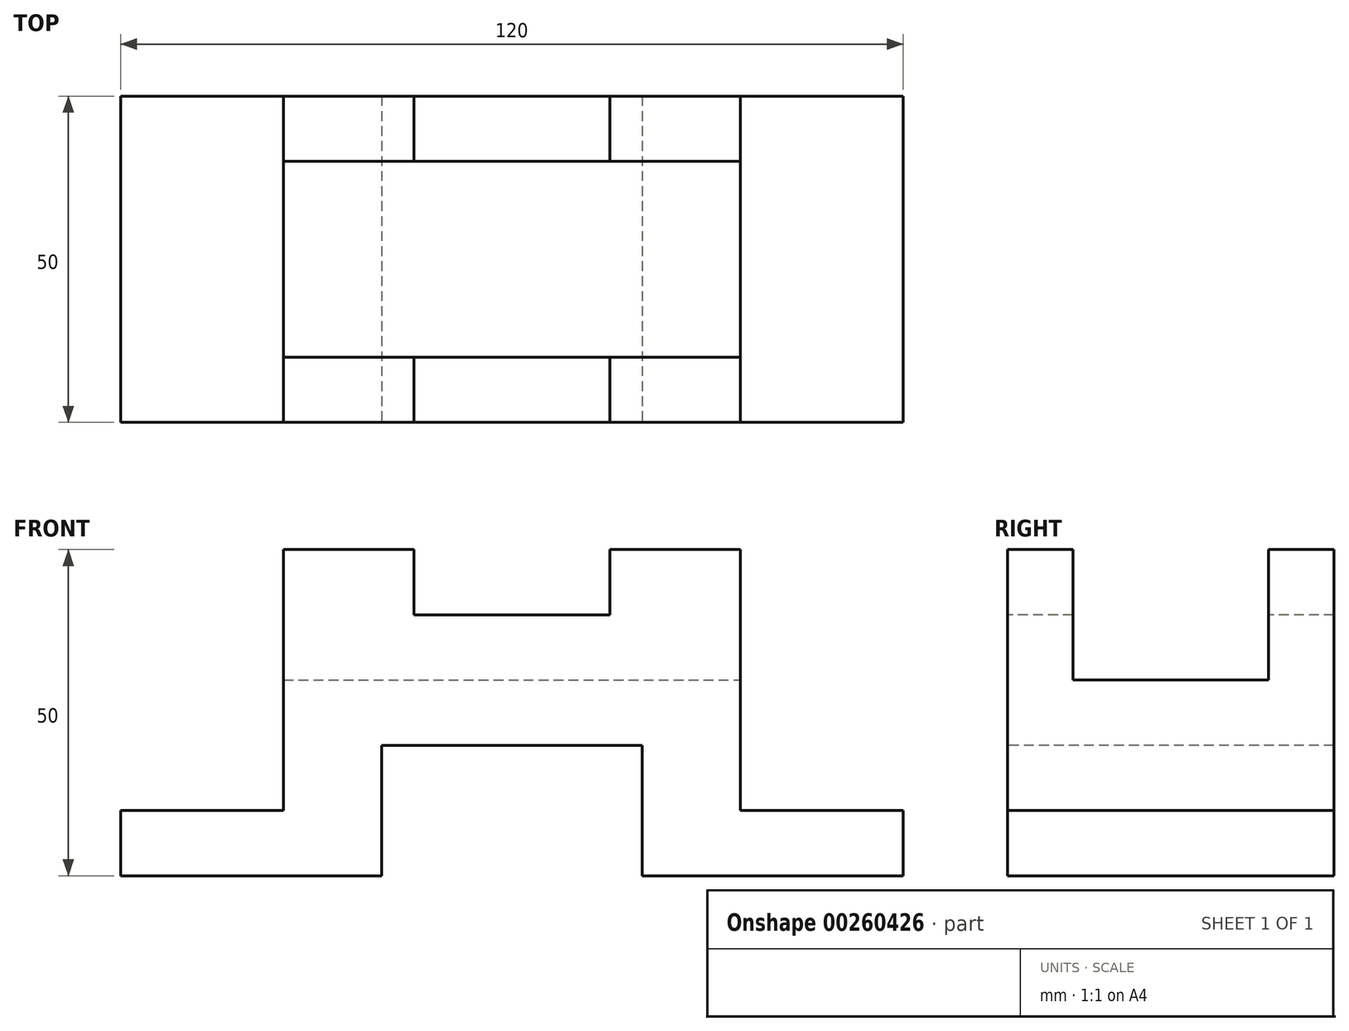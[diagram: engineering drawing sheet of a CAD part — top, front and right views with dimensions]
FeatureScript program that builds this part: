
annotation { "Feature Type Name" : "Feature", "Feature Type Description" : "" }
export const myFeature = defineFeature(function(context is Context, id is Id, definition is map)
    precondition{}
    {
        {
            assignVariable(context, id + "F0", {"name" : "A", "anyValue" : 50});
        }
        {
            var Q0;
            Q0=qCreatedBy(makeId("Front.planeOp"),FACE);
            var sketch = newSketch(context, id + "F1", { "sketchPlane" : qUnion([Q0])});
            skLineSegment(sketch, "E0.bottom", {"start": v(60, 25) * mm, "end": v(-60, 25) * mm});
            skLineSegment(sketch, "E0.top", {"start": v(60, -25) * mm, "end": v(-60, -25) * mm});
            skLineSegment(sketch, "E0.left", {"start": v(60, 25) * mm, "end": v(60, -25) * mm});
            skLineSegment(sketch, "E0.right", {"start": v(-60, 25) * mm, "end": v(-60, -25) * mm});
            skPoint(sketch, "E0.middle", {"position": v(0, 0) * mm});
            skSolve(sketch);
        }
        {
            var Q0;
            Q0=makeQuery(id+"F1.imprint","IMPRINT",FACE,{"disambiguationData":[TD([[makeQuery(id+"F1.imprint","IMPRINT",EDGE,{"derivedFrom":sQuery(id+"F1.wireOp",EDGE,"E0.bottom")}),1.0]])]});
            extrude(context, id + "F2", {"entities" : qUnion([Q0]), "depth" : (getVariable(context, 'A')) * mm});
        }
        {
            var Q0;
            Q0=makeQuery(id+"F2.opExtrude","CAP_FACE",FACE,{"disambiguationData":[OSD([sQuery(id+"F1.wireOp",EDGE,"E0.bottom"),sQuery(id+"F1.wireOp",EDGE,"E0.top"),sQuery(id+"F1.wireOp",EDGE,"E0.left"),sQuery(id+"F1.wireOp",EDGE,"E0.right")])],"isStart":false});
            var sketch = newSketch(context, id + "F3", { "sketchPlane" : qUnion([Q0])});
            skLineSegment(sketch, "E1.bottom", {"start": v(60, 25) * mm, "end": v(35, 25) * mm});
            skLineSegment(sketch, "E1.top", {"start": v(60, -15) * mm, "end": v(35, -15) * mm});
            skLineSegment(sketch, "E1.left", {"start": v(60, 25) * mm, "end": v(60, -15) * mm});
            skLineSegment(sketch, "E1.right", {"start": v(35, 25) * mm, "end": v(35, -15) * mm});
            skLineSegment(sketch, "E2.MirrorCS", {"start": v(-35, 25) * mm, "end": v(-35, -15) * mm});
            skLineSegment(sketch, "E3.MirrorCS", {"start": v(-60, 25) * mm, "end": v(-35, 25) * mm});
            skLineSegment(sketch, "E4.MirrorCS", {"start": v(-60, 25) * mm, "end": v(-60, -15) * mm});
            skLineSegment(sketch, "E5.MirrorCS", {"start": v(-60, -15) * mm, "end": v(-35, -15) * mm});
            skLineSegment(sketch, "E6.bottom", {"start": v(15, 15) * mm, "end": v(-15, 15) * mm});
            skLineSegment(sketch, "E6.left", {"start": v(15, 15) * mm, "end": v(15, 25) * mm});
            skLineSegment(sketch, "E6.right", {"start": v(-15, 15) * mm, "end": v(-15, 25) * mm});
            skPoint(sketch, "E6.middle", {"position": v(0, 25) * mm});
            skLineSegment(sketch, "E7", {"start": v(-15, 25) * mm, "end": v(15, 25) * mm});
            skPoint(sketch, "E8.orphan", {"position": v(-15, 35) * mm});
            skPoint(sketch, "E9.orphan", {"position": v(15, 35) * mm});
            skLineSegment(sketch, "E10.bottom", {"start": v(20, -5) * mm, "end": v(-20, -5) * mm});
            skLineSegment(sketch, "E10.left", {"start": v(20, -5) * mm, "end": v(20, -25) * mm});
            skLineSegment(sketch, "E10.right", {"start": v(-20, -5) * mm, "end": v(-20, -25) * mm});
            skPoint(sketch, "E10.middle", {"position": v(0, -25) * mm});
            skLineSegment(sketch, "E11", {"start": v(-20, -25) * mm, "end": v(20, -25) * mm});
            skPoint(sketch, "E10.top.end.orphan", {"position": v(-20, -45) * mm});
            skPoint(sketch, "E12.orphan", {"position": v(20, -45) * mm});
            skSolve(sketch);
        }
        {
            var Q0;
            Q0=makeQuery(id+"F3.imprint","IMPRINT",FACE,{"disambiguationData":[TD([[makeQuery(id+"F3.imprint","IMPRINT",EDGE,{"derivedFrom":sQuery(id+"F3.wireOp",EDGE,"E2.MirrorCS")}),-1.0]])]});
            var Q1;
            Q1=makeQuery(id+"F3.imprint","IMPRINT",FACE,{"disambiguationData":[TD([[makeQuery(id+"F3.imprint","IMPRINT",EDGE,{"derivedFrom":sQuery(id+"F3.wireOp",EDGE,"E6.bottom")}),-1.0]])]});
            var Q2;
            Q2=makeQuery(id+"F3.imprint","IMPRINT",FACE,{"disambiguationData":[TD([[makeQuery(id+"F3.imprint","IMPRINT",EDGE,{"derivedFrom":sQuery(id+"F3.wireOp",EDGE,"E1.bottom")}),1.0]])]});
            var Q3;
            Q3=makeQuery(id+"F3.imprint","IMPRINT",FACE,{"disambiguationData":[TD([[makeQuery(id+"F3.imprint","IMPRINT",EDGE,{"derivedFrom":sQuery(id+"F3.wireOp",EDGE,"E10.bottom")}),1.0]])]});
            extrude(context, id + "F4", {"entities" : qUnion([Q0, Q1, Q2, Q3]), "operationType" : NewBodyOperationType.REMOVE, "endBound" : BoundingType.UP_TO_NEXT, "oppositeDirection" : true, "depth" : 25 * mm});
        }
        {
            var Q0;
            Q0=makeQuery(id+"F4.boolean.opBoolean","COPY",FACE,{"derivedFrom":makeQuery(id+"F4.opExtrude","SWEPT_FACE",FACE,{"disambiguationData":[OSD([sQuery(id+"F3.wireOp",EDGE,"E1.right")])]})});
            var sketch = newSketch(context, id + "F5", { "sketchPlane" : qUnion([Q0])});
            skLineSegment(sketch, "E13.bottom", {"start": v(-10, 5) * mm, "end": v(-40, 5) * mm});
            skLineSegment(sketch, "E13.left", {"start": v(-10, 5) * mm, "end": v(-10, 25) * mm});
            skLineSegment(sketch, "E13.right", {"start": v(-40, 5) * mm, "end": v(-40, 25) * mm});
            skPoint(sketch, "E13.middle", {"position": v(-25, 25) * mm});
            skLineSegment(sketch, "E14", {"start": v(-40, 25) * mm, "end": v(-10, 25) * mm});
            skPoint(sketch, "E15.orphan", {"position": v(-40, 45) * mm});
            skPoint(sketch, "E16.orphan", {"position": v(-10, 45) * mm});
            skSolve(sketch);
        }
        {
            var Q0;
            Q0=makeQuery(id+"F5.imprint","IMPRINT",FACE,{"disambiguationData":[TD([[makeQuery(id+"F5.imprint","IMPRINT",EDGE,{"derivedFrom":sQuery(id+"F5.wireOp",EDGE,"E13.bottom")}),-1.0]])]});
            extrude(context, id + "F6", {"entities" : qUnion([Q0]), "operationType" : NewBodyOperationType.REMOVE, "endBound" : BoundingType.THROUGH_ALL, "oppositeDirection" : true, "depth" : 25 * mm});
        }
    });
